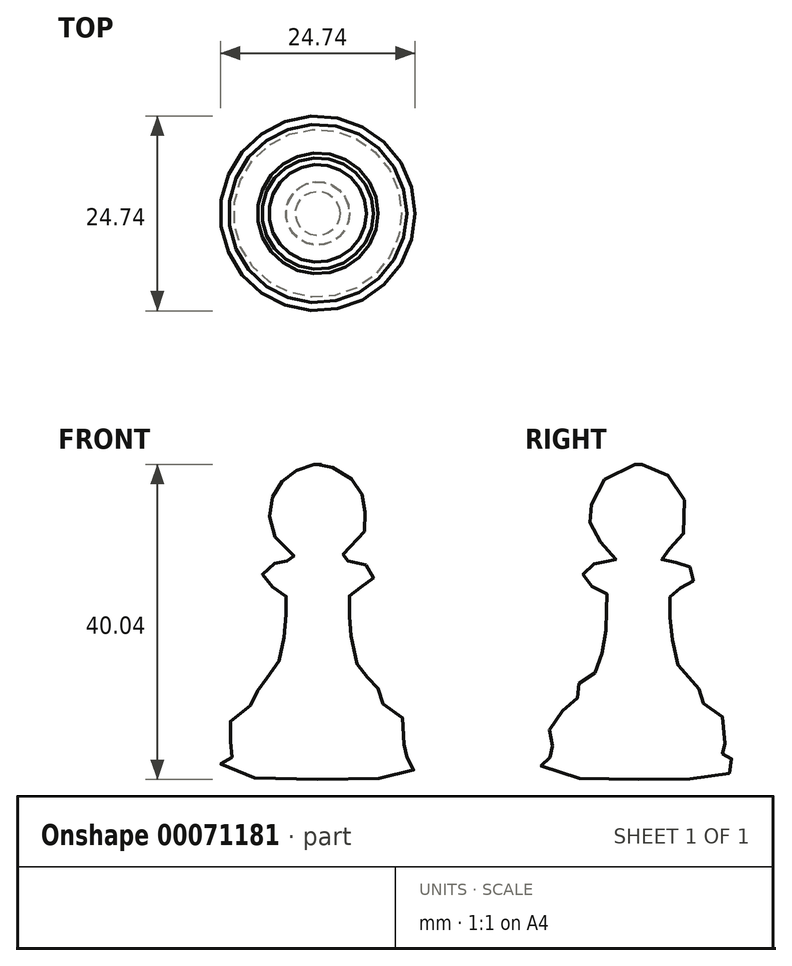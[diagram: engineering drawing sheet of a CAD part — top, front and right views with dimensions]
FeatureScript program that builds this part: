
annotation { "Feature Type Name" : "Feature", "Feature Type Description" : "" }
export const myFeature = defineFeature(function(context is Context, id is Id, definition is map)
    precondition{}
    {
        {
            var Q0;
            Q0=qCreatedBy(makeId("Front.planeOp"),FACE);
            var sketch = newSketch(context, id + "F0", { "sketchPlane" : qUnion([Q0])});
            skLineSegment(sketch, "E0", {"start": v(0, 15.34) * mm, "end": v(0, -24.66) * mm});
            skPoint(sketch, "E1.1.internal.orphan", {"position": v(1.4, -27.67) * mm});
            skPoint(sketch, "E1.2.internal.orphan", {"position": v(3.48, -27.67) * mm});
            skPoint(sketch, "E1.26.internal.orphan", {"position": v(6.24, 0) * mm});
            skFitSpline(sketch, "E2", {"points": [v(0, 15.34) * mm, v(0.9, 15.34) * mm, v(3.33, 14.23) * mm, v(5.04, 12.62) * mm, v(5.85, 10.9) * mm, v(6.05, 9.08) * mm, v(5.85, 6.76) * mm, v(2.82, 3.42) * mm, v(3.23, 3.22) * mm, v(5.25, 2.82) * mm, v(6.56, 2.31) * mm, v(7.06, 0.9) * mm, v(6.24, 0) * mm, v(4.14, -0.82) * mm, v(4.03, -1.53) * mm, v(4.03, -4.15) * mm, v(4.24, -6.27) * mm, v(5.25, -10.62) * mm, v(6.24, -11.63) * mm, v(7.57, -12.54) * mm, v(7.67, -14.05) * mm, v(8.88, -15.47) * mm, v(11.3, -17.9) * mm, v(10.7, -21.73) * mm, v(11.61, -21.93) * mm, v(12.32, -23.25) * mm, v(0, -24.66) * mm], "startDerivative": vector(31.67, 4.54) * mm, "endDerivative": vector(-191.06, -0.24) * mm});
            skPoint(sketch, "E3.orphan", {"position": v(0, -27.67) * mm});
            skSolve(sketch);
        }
        {
            var Q0;
            Q0 = qSketchRegion(id + "F0", true);
            var Q1;
            Q1=sQuery(id+"F0.wireOp",EDGE,"E0");
            revolve(context, id + "F1", {"entities" : qUnion([Q0]), "axis" : qUnion([Q1]), "revolveType" : RevolveType.FULL});
        }
    });
